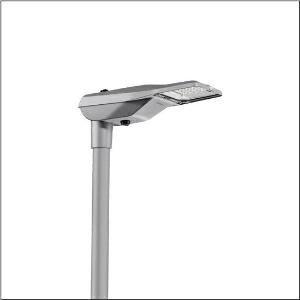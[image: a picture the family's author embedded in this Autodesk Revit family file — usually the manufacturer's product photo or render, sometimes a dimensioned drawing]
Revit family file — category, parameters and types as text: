
# Revit family: streetlight_sl_21_micro___stw1_0a_5xe1e43t08db_d620
name_source: partatom
category: Lighting Fixtures
units: mm (PartAtom-declared; Revit-internal decimal feet)

## family parameters
Cut with Voids When Loaded = No
Host = Face
Light Source = No
Part Type = Normal
Room Calculation Point = No
Round Connector Dimension = Use Diameter
Shared = No

## types (1)
- --- (1 x LED, 5320 lm, 39.1 W, 4000K)
    Apparent Load = 39 VA
    CIE Flux Codes = 38 75 98 100 100
    Color Rendering = 70
    Color Temperature = 4000K
    Default Elevation = 1800 mm
    Description = Streetlight SL 21 micro, mast luminaire, primary light control with lens, of PMMA, primary optical cover: cover, of toughened safety glass, transparent, light distribution: STW1.0a, light emission: direct distribution, primary light characteristic: asymmetric, installation type: side-entry, post-top, LED, High Power LED, rated luminous flux: 5.320lm, luminous efficacy: 136lm/W, light colour: 740, colour temperature: 4000K, control: flexible luminous flux parameterisation, time-dependent luminous flux control, constant luminous flux control, overheat protection, presetting dimming logarithmic, mains connection: 220..240V, AC, 50/60Hz, start of lifetime: 39W, end of service life: 41W, reduction: 18W, luminaire housing, of diecast aluminium, powder-coated, Siteco® metallic grey (DB 702S), corrosivity category C5 mid according to DIN EN ISO 12944, please order mast flange separately, inclination adjustable: 0°, 5°, 10°, 15°, sealing non-destructively replaceable, multi-level sealing system, length: 528mm, width: 235mm, height: 110mm, mast flange for spigot size: 42mm (side-entry): 5XC10008XM4, 60/48mm (side-entry/post-top): 5XC10108XM2, 76/60mm (side-entry/post-top): 5XC10108XM1, Smart Interface below and above, protection rating (complete): IP66, insulation class (complete): insulation class II (safety insulation), certification: CE, ENEC, ENEC+, VDE, impact resistance: IK09, permissible operating ambient temperature for outdoor applications: -40..+50°C, standard-compliant lighting for roads and squares, packaging unit: 1 piece

Light Distribution: STW1.0a
    Height = 110 mm
    Lamp = 1 x LED
    Lamp Light Flux = 5320 lm
    Lamp Power = 39.1 W
    Lamp count = 1
    Length = 528 mm
    Luminous efficacy = 136 lm/W
    Manufacturer = Siteco
    ModVariant = No
    Model = 5XE1E43T08DB
    Number of Poles = 1
    OnlyDefault = Yes
    Power Factor = 1
    Product Name = Streetlight SL 21 micro | STW1.0a
    Product group = mast luminaire | pylon top
    ProductGroupID = 6100
    Protection Class = Protection class II
    Protection Degree = IP 66
    RLX_Detail_Level = 1
    RLX_Emergency_Light_Flux = 0 lm
    RLX_Emergency_Type = 0
    RLX_Emergency_Type_DB = No
    RlxData = <blob elided: 98185 chars, md5=319478fc>
    Socket = socket
    Standby Power = 0 W
    System Light Flux = 5320 lm
    System Power = 39 W
    Type Comments = factory setting: luminous flux: 100 % | dim-lin: 254 | 765 mA
    Type Image = l_1007239.jpg
    URL = http://relux.com
    VarID = @adj_105389
    Voltage = 0 V
    Weight = 0.00 kg
    Width = 235 mm

## geometry (parser evidence)
native form markers: Blend x4, Sweep x9
no freeform markers — native parametric forms only
